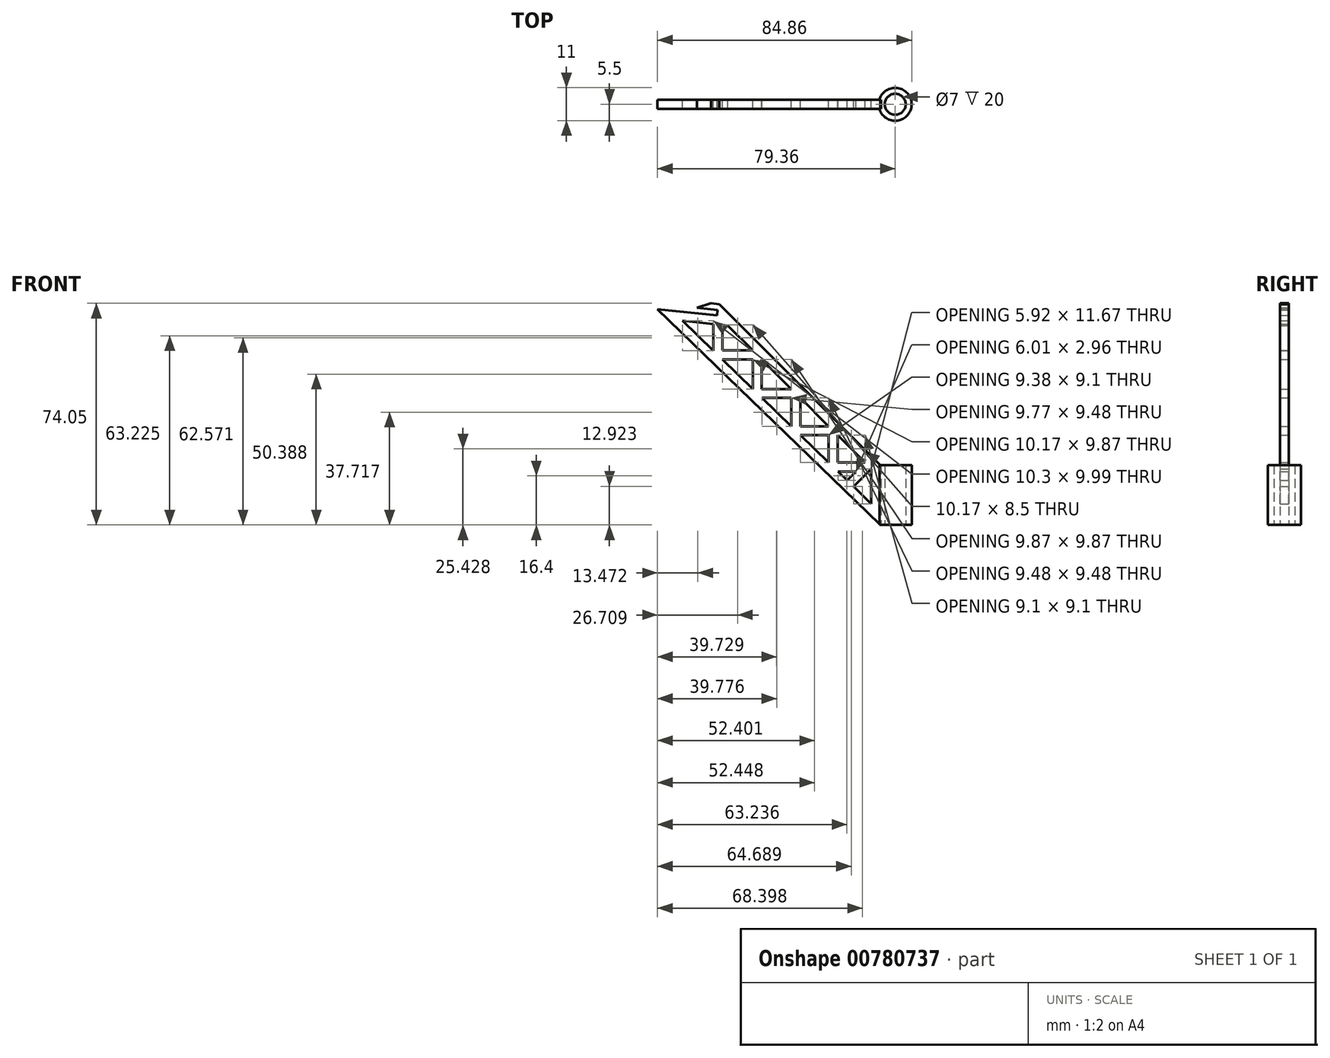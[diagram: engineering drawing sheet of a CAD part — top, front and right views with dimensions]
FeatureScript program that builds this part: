
annotation { "Feature Type Name" : "Feature", "Feature Type Description" : "" }
export const myFeature = defineFeature(function(context is Context, id is Id, definition is map)
    precondition{}
    {
        {
            var Q0;
            Q0=qCreatedBy(makeId("Top.planeOp"),FACE);
            var sketch = newSketch(context, id + "F0", { "sketchPlane" : qUnion([Q0])});
            skCircle(sketch, "E0", {"center": v(0, 0) * mm, "radius": 3.5 * mm});
            skArc(sketch, "E1", {"start": v(-5.3, -1.5) * mm, "mid": v(5.5, 0) * mm, "end": v(-5.3, 1.5) * mm});
            skLineSegment(sketch, "E2", {"start": v(-5.3, 1.5) * mm, "end": v(-4.8, 1.5) * mm});
            skLineSegment(sketch, "E3", {"start": v(-4.8, 1.5) * mm, "end": v(-4.8, -1.5) * mm});
            skLineSegment(sketch, "E4", {"start": v(-4.8, -1.5) * mm, "end": v(-5.3, -1.5) * mm});
            skSolve(sketch);
        }
        {
            var Q0;
            Q0=makeQuery(id+"F0.imprint","IMPRINT",FACE,{"disambiguationData":[TD([[makeQuery(id+"F0.imprint","IMPRINT",EDGE,{"derivedFrom":sQuery(id+"F0.wireOp",EDGE,"E0")}),-1.0]])]});
            extrude(context, id + "F1", {"entities" : qUnion([Q0]), "depth" : 20 * mm, "offsetDistance" : 25 * mm});
        }
        {
            var Q0;
            Q0=qCreatedBy(makeId("Front.planeOp"),FACE);
            var sketch = newSketch(context, id + "F2", { "sketchPlane" : qUnion([Q0])});
            skLineSegment(sketch, "E5", {"start": v(-5, 0) * mm, "end": v(-79.36, 72.11) * mm});
            skLineSegment(sketch, "E6", {"start": v(-79.36, 72.11) * mm, "end": v(-54.5, 69.5) * mm});
            skLineSegment(sketch, "E7", {"start": v(-54.5, 69.5) * mm, "end": v(-5, 20) * mm});
            skLineSegment(sketch, "E8", {"start": v(-5, 20) * mm, "end": v(-5, 0) * mm});
            skLineSegment(sketch, "E9", {"start": v(-55.87, 66.62) * mm, "end": v(-8, 18.76) * mm});
            skLineSegment(sketch, "E10", {"start": v(-8, 18.76) * mm, "end": v(-8, 7.09) * mm});
            skLineSegment(sketch, "E11", {"start": v(-8, 7.09) * mm, "end": v(-71.04, 68.22) * mm});
            skLineSegment(sketch, "E12", {"start": v(-71.04, 68.22) * mm, "end": v(-55.87, 66.62) * mm});
            skLineSegment(sketch, "E13", {"start": v(-8, 18.76) * mm, "end": v(-13.92, 12.83) * mm});
            skLineSegment(sketch, "E14", {"start": v(-13.92, 12.83) * mm, "end": v(-16.08, 14.92) * mm});
            skLineSegment(sketch, "E15", {"start": v(-16.08, 14.92) * mm, "end": v(-13.12, 17.88) * mm});
            skLineSegment(sketch, "E16", {"start": v(-10.12, 20.88) * mm, "end": v(-19.22, 20.88) * mm});
            skLineSegment(sketch, "E17", {"start": v(-22.22, 20.88) * mm, "end": v(-22.22, 29.98) * mm});
            skLineSegment(sketch, "E18", {"start": v(-22.22, 32.98) * mm, "end": v(-31.7, 32.98) * mm});
            skLineSegment(sketch, "E19", {"start": v(-34.7, 32.98) * mm, "end": v(-34.7, 42.46) * mm});
            skLineSegment(sketch, "E20", {"start": v(-34.7, 45.46) * mm, "end": v(-44.56, 45.46) * mm});
            skLineSegment(sketch, "E21", {"start": v(-47.56, 45.46) * mm, "end": v(-47.56, 55.32) * mm});
            skLineSegment(sketch, "E22", {"start": v(-47.56, 58.32) * mm, "end": v(-57.74, 58.32) * mm});
            skLineSegment(sketch, "E23", {"start": v(-13.12, 17.88) * mm, "end": v(-19.13, 17.88) * mm});
            skLineSegment(sketch, "E24", {"start": v(-47.56, 55.32) * mm, "end": v(-57.74, 55.32) * mm});
            skLineSegment(sketch, "E25", {"start": v(-57.74, 58.32) * mm, "end": v(-57.74, 66.82) * mm});
            skLineSegment(sketch, "E26", {"start": v(-44.56, 45.46) * mm, "end": v(-44.56, 55.32) * mm});
            skLineSegment(sketch, "E27", {"start": v(-34.7, 42.46) * mm, "end": v(-44.47, 42.46) * mm});
            skLineSegment(sketch, "E28", {"start": v(-31.7, 32.98) * mm, "end": v(-31.7, 42.46) * mm});
            skLineSegment(sketch, "E29", {"start": v(-22.22, 29.98) * mm, "end": v(-31.6, 29.98) * mm});
            skLineSegment(sketch, "E30", {"start": v(-19.22, 20.88) * mm, "end": v(-19.22, 29.98) * mm});
            skLineSegment(sketch, "E31", {"start": v(-55.87, 66.62) * mm, "end": v(-55.87, 66.62) * mm});
            skLineSegment(sketch, "E32", {"start": v(-60.74, 67.14) * mm, "end": v(-60.74, 58.23) * mm});
            skLineSegment(sketch, "E33", {"start": v(-54.5, 69.5) * mm, "end": v(-58.77, 73.77) * mm});
            skLineSegment(sketch, "E34", {"start": v(-58.77, 73.77) * mm, "end": v(-61.48, 74.05) * mm});
            skLineSegment(sketch, "E35", {"start": v(-61.48, 74.05) * mm, "end": v(-66.24, 72.54) * mm});
            skLineSegment(sketch, "E36", {"start": v(-66.24, 72.54) * mm, "end": v(-59.28, 71.81) * mm});
            skLineSegment(sketch, "E37", {"start": v(-59.28, 71.81) * mm, "end": v(-59.47, 70.02) * mm});
            skSolve(sketch);
        }
        {
            var Q0;
            Q0=makeQuery(id+"F2.imprint","IMPRINT",FACE,{"disambiguationData":[TD([[makeQuery(id+"F2.imprint","IMPRINT",EDGE,{"derivedFrom":sQuery(id+"F2.wireOp",EDGE,"E5")}),-1.0]])]});
            var Q1;
            {var subQ8=sQuery(id+"F2.wireOp",EDGE,"E13");Q1=makeQuery(id+"F2.imprint","IMPRINT",FACE,{"disambiguationData":[TD([[makeQuery(id+"F2.imprint","IMPRINT",EDGE,{"derivedFrom":subQ8}),-1.0]])]});}
            var Q2;
            {var subQ0=sQuery(id+"F2.wireOp",EDGE,"ld9xTmED-HSJg-OcN6-DF6Q-gvQvIEZLsroh");Q2=makeQuery(id+"F2.imprint","IMPRINT",FACE,{"disambiguationData":[TD([[makeQuery(id+"F2.imprint","IMPRINT",EDGE,{"derivedFrom":subQ0}),1.0]])]});}
            var Q3;
            {var subQ0=sQuery(id+"F2.wireOp",EDGE,"E33");Q3=makeQuery(id+"F2.imprint","IMPRINT",FACE,{"disambiguationData":[TD([[makeQuery(id+"F2.imprint","IMPRINT",EDGE,{"derivedFrom":subQ0}),1.0]])]});}
            extrude(context, id + "F3", {"entities" : qUnion([Q0, Q1, Q2, Q3]), "depth" : 3 * mm, "offsetDistance" : 25 * mm, "symmetric" : true});
        }
    });
